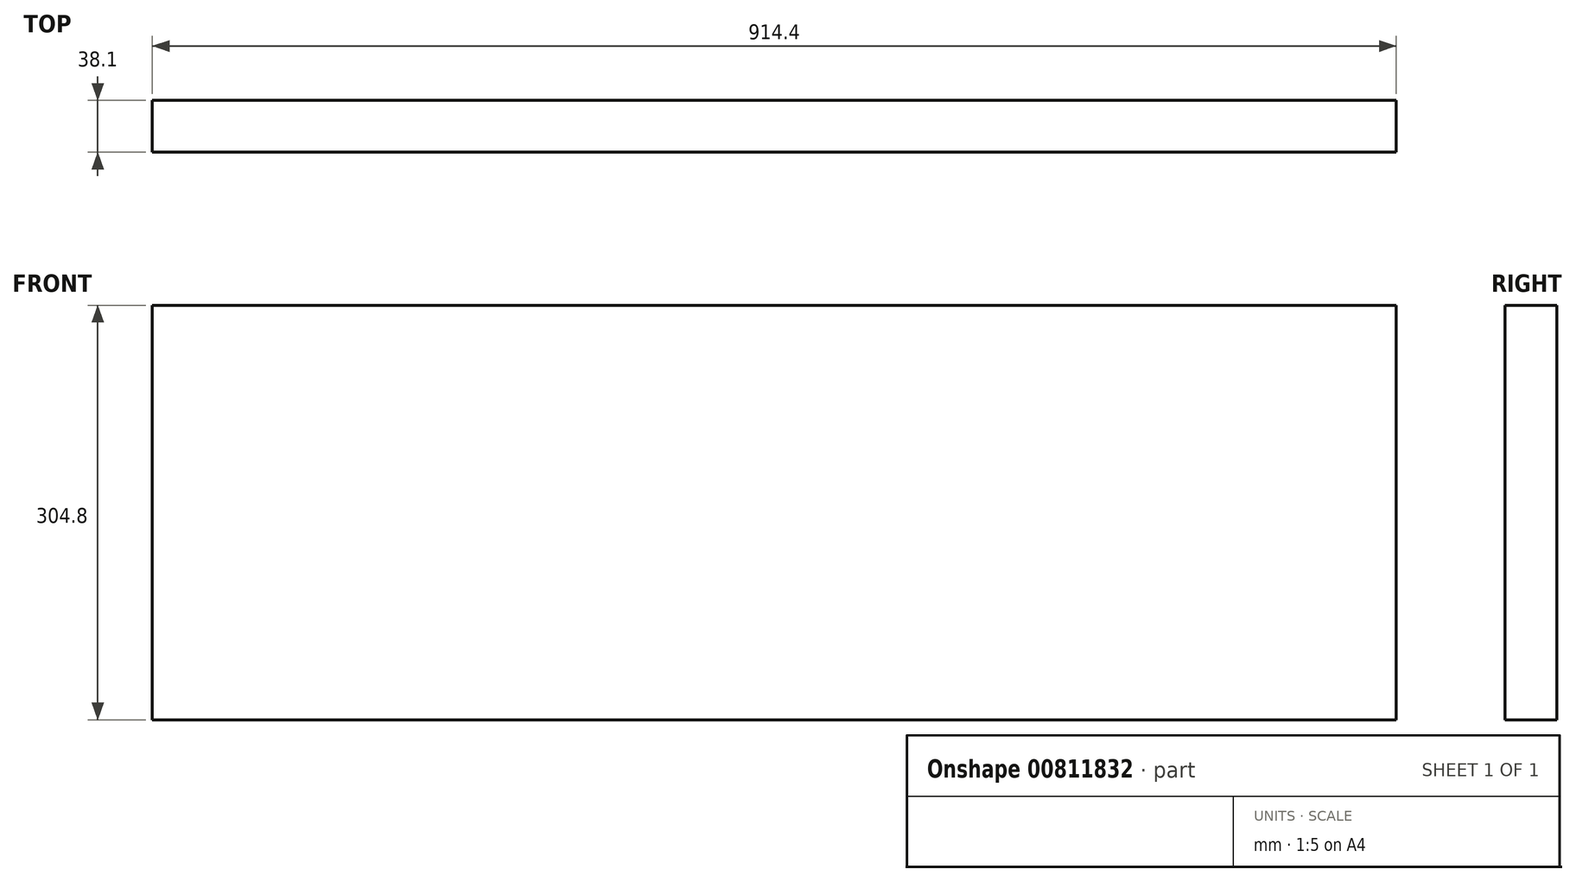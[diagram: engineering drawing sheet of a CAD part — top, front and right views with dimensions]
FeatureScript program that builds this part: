
annotation { "Feature Type Name" : "Feature", "Feature Type Description" : "" }
export const myFeature = defineFeature(function(context is Context, id is Id, definition is map)
    precondition{}
    {
        {
            var Q0;
            Q0=qCreatedBy(makeId("Front.planeOp"),FACE);
            var sketch = newSketch(context, id + "F0", { "sketchPlane" : qUnion([Q0])});
            skLineSegment(sketch, "E0.bottom", {"start": v(-445.53, 240.58) * mm, "end": v(468.87, 240.58) * mm});
            skLineSegment(sketch, "E0.top", {"start": v(-445.53, -64.22) * mm, "end": v(468.87, -64.22) * mm});
            skLineSegment(sketch, "E0.left", {"start": v(-445.53, 240.58) * mm, "end": v(-445.53, -64.22) * mm});
            skLineSegment(sketch, "E0.right", {"start": v(468.87, 240.58) * mm, "end": v(468.87, -64.22) * mm});
            skSolve(sketch);
        }
        {
            var Q0;
            Q0 = qSketchRegion(id + "F0", true);
            extrude(context, id + "F1", {"entities" : qUnion([Q0]), "endBound" : BoundingType.SYMMETRIC, "depth" : 38.1 * mm, "offsetDistance" : 25.4 * mm});
        }
    });
